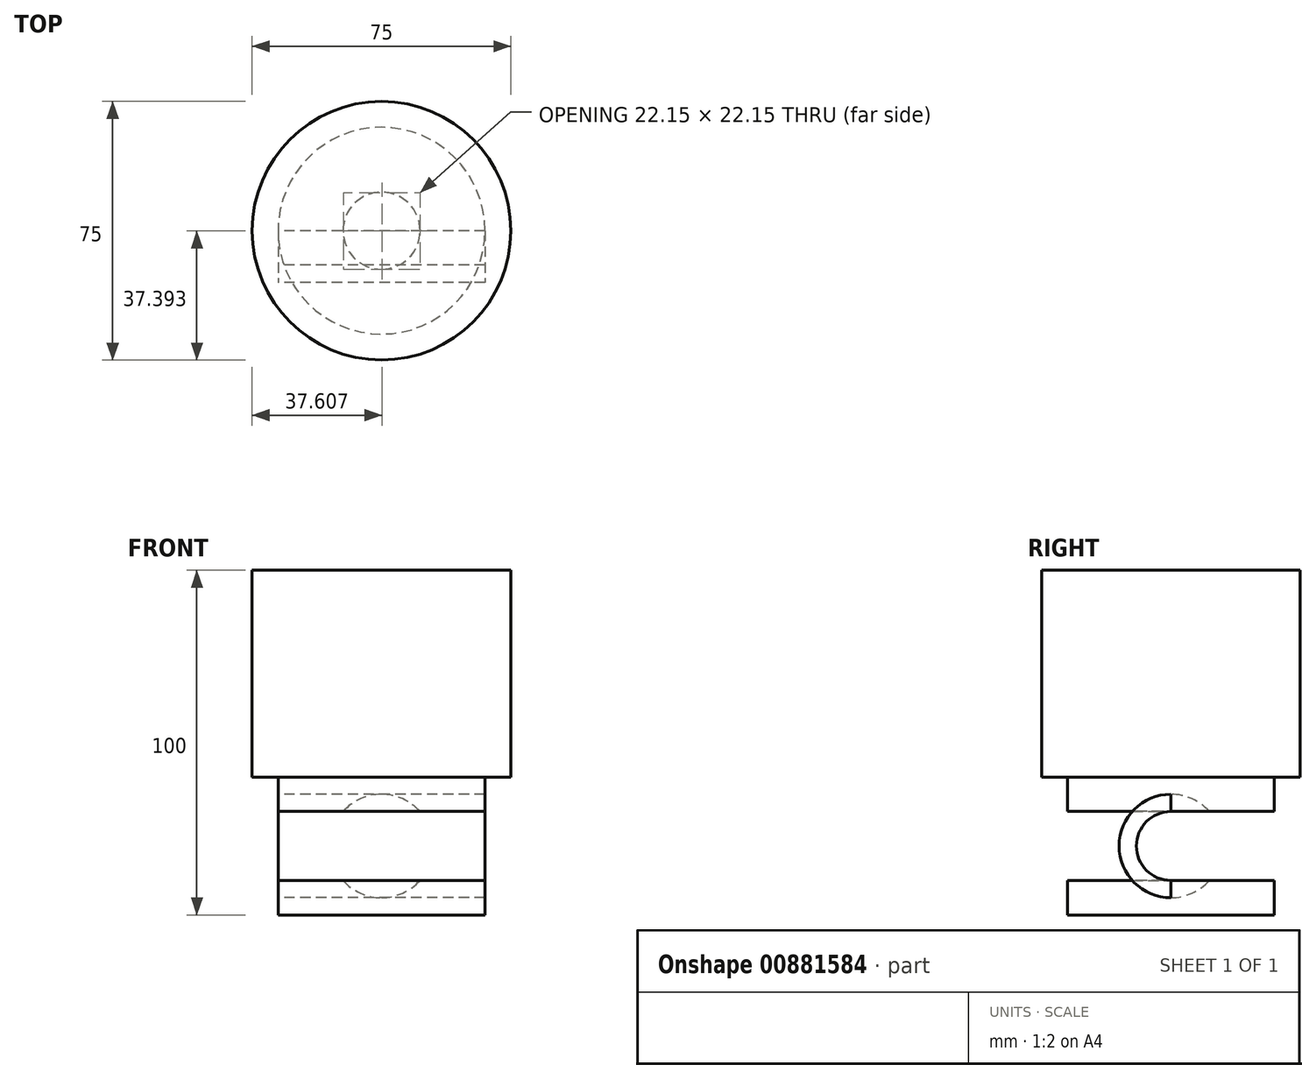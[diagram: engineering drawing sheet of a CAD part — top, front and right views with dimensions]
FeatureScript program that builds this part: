
annotation { "Feature Type Name" : "Feature", "Feature Type Description" : "" }
export const myFeature = defineFeature(function(context is Context, id is Id, definition is map)
    precondition{}
    {
        {
            var Q0;
            Q0=qCreatedBy(makeId("Top.planeOp"),FACE);
            var sketch = newSketch(context, id + "F0", { "sketchPlane" : qUnion([Q0])});
            skCircle(sketch, "E0", {"center": v(0, 0) * mm, "radius": 37.5 * mm});
            skCircle(sketch, "E1.0", {"center": v(0, 0) * mm, "radius": 32.5 * mm});
            skSolve(sketch);
        }
        {
            var Q0;
            Q0=makeQuery(id+"F0.imprint","IMPRINT",FACE,{"disambiguationData":[TD([[makeQuery(id+"F0.imprint","IMPRINT",EDGE,{"derivedFrom":sQuery(id+"F0.wireOp",EDGE,"E1.0")}),1.0]])]});
            var Q1;
            Q1=makeQuery(id+"F0.imprint","IMPRINT",FACE,{"disambiguationData":[TD([[makeQuery(id+"F0.imprint","IMPRINT",EDGE,{"derivedFrom":sQuery(id+"F0.wireOp",EDGE,"E0")}),1.0]])]});
            var Q2;
            Q2=sQuery(id+"F0.wireOp",EDGE,"E0");
            extrude(context, id + "F1", {"entities" : qUnion([Q0, Q1]), "surfaceEntities" : qUnion([Q2]), "depth" : 60 * mm, "offsetDistance" : 25 * mm});
        }
        {
            var Q0;
            Q0=qCreatedBy(makeId("Right.planeOp"),FACE);
            var sketch = newSketch(context, id + "F2", { "sketchPlane" : qUnion([Q0])});
            skLineSegment(sketch, "E2", {"start": v(0, 0) * mm, "end": v(0, -20) * mm});
            skCircle(sketch, "E3", {"center": v(0, -20) * mm, "radius": 10 * mm});
            skCircle(sketch, "E4.0", {"center": v(0, -20) * mm, "radius": 15 * mm});
            skLineSegment(sketch, "E5", {"start": v(0, 0) * mm, "end": v(0, -10) * mm});
            skLineSegment(sketch, "E6", {"start": v(0, -10) * mm, "end": v(-30, -10) * mm});
            skLineSegment(sketch, "E7", {"start": v(-30, -10) * mm, "end": v(-30, 0) * mm});
            skLineSegment(sketch, "E8", {"start": v(-30, 0) * mm, "end": v(0, 0) * mm});
            skLineSegment(sketch, "E9", {"start": v(0, -20) * mm, "end": v(0, -40) * mm});
            skLineSegment(sketch, "E10", {"start": v(0, -40) * mm, "end": v(-30, -40) * mm});
            skLineSegment(sketch, "E11", {"start": v(-30, -40) * mm, "end": v(-30, -30) * mm});
            skLineSegment(sketch, "E12", {"start": v(-30, -30) * mm, "end": v(0, -30) * mm});
            skLineSegment(sketch, "E13", {"start": v(0, -30) * mm, "end": v(0, -40) * mm});
            skSolve(sketch);
        }
        {
            var Q0;
            {var subQ0=sQuery(id+"F2.wireOp",EDGE,"E7");Q0=makeQuery(id+"F2.imprint","IMPRINT",FACE,{"disambiguationData":[TD([[makeQuery(id+"F2.imprint","IMPRINT",EDGE,{"derivedFrom":subQ0}),-1.0]])]});}
            var Q1;
            {var subQ6=sQuery(id+"F2.wireOp",EDGE,"E10");Q1=makeQuery(id+"F2.imprint","IMPRINT",FACE,{"disambiguationData":[TD([[makeQuery(id+"F2.imprint","IMPRINT",EDGE,{"derivedFrom":subQ6}),-1.0]])]});}
            var Q2;
            Q2=sQuery(id+"F2.wireOp",EDGE,"E2");
            revolve(context, id + "F3", {"operationType" : NewBodyOperationType.ADD, "surfaceOperationType" : NewSurfaceOperationType.NEW, "entities" : qUnion([Q0, Q1]), "axis" : qUnion([Q2]), "revolveType" : RevolveType.FULL});
        }
        {
            var Q0;
            {var subQ0=sQuery(id+"F2.wireOp",EDGE,"E6");var subQ1=sQuery(id+"F2.wireOp",EDGE,"E4.0");var subQ2=makeQuery(id+"F2.imprint","INTERSECT",VERTEX,{"derivedFrom":[subQ1,subQ0]});Q0=makeQuery(id+"F2.imprint","IMPRINT",FACE,{"disambiguationData":[TD([[makeQuery(id+"F2.imprint","IMPRINT",EDGE,{"disambiguationData":[TD([[subQ2,1.0]])],"derivedFrom":subQ1}),1.0]])]});}
            var Q1;
            {var subQ0=sQuery(id+"F2.wireOp",EDGE,"E6");var subQ5=sQuery(id+"F2.wireOp",EDGE,"E4.0");var subQ6=makeQuery(id+"F2.imprint","INTERSECT",VERTEX,{"derivedFrom":[subQ5,subQ0]});Q1=makeQuery(id+"F2.imprint","IMPRINT",FACE,{"disambiguationData":[TD([[makeQuery(id+"F2.imprint","IMPRINT",EDGE,{"disambiguationData":[TD([[subQ6,-1.0]])],"derivedFrom":subQ5}),1.0]])]});}
            var Q2;
            {var subQ0=sQuery(id+"F2.wireOp",EDGE,"E12");var subQ1=sQuery(id+"F2.wireOp",EDGE,"E4.0");var subQ2=makeQuery(id+"F2.imprint","INTERSECT",VERTEX,{"derivedFrom":[subQ1,subQ0]});Q2=makeQuery(id+"F2.imprint","IMPRINT",FACE,{"disambiguationData":[TD([[makeQuery(id+"F2.imprint","IMPRINT",EDGE,{"disambiguationData":[TD([[subQ2,-1.0]])],"derivedFrom":subQ1}),1.0]])]});}
            var Q3;
            {var subQ0=sQuery(id+"F2.wireOp",EDGE,"E5");var subQ5=sQuery(id+"F2.wireOp",EDGE,"E4.0");var subQ6=makeQuery(id+"F2.imprint","INTERSECT",VERTEX,{"derivedFrom":[subQ5,subQ0]});Q3=makeQuery(id+"F2.imprint","IMPRINT",FACE,{"disambiguationData":[TD([[makeQuery(id+"F2.imprint","IMPRINT",EDGE,{"disambiguationData":[TD([[subQ6,1.0]])],"derivedFrom":subQ5}),1.0]])]});}
            extrude(context, id + "F4", {"entities" : qUnion([Q0, Q1, Q2, Q3]), "depth" : 30 * mm, "offsetDistance" : 25 * mm, "hasSecondDirection" : true, "secondDirectionOppositeDirection" : true, "secondDirectionDepth" : 30 * mm});
        }
    });
